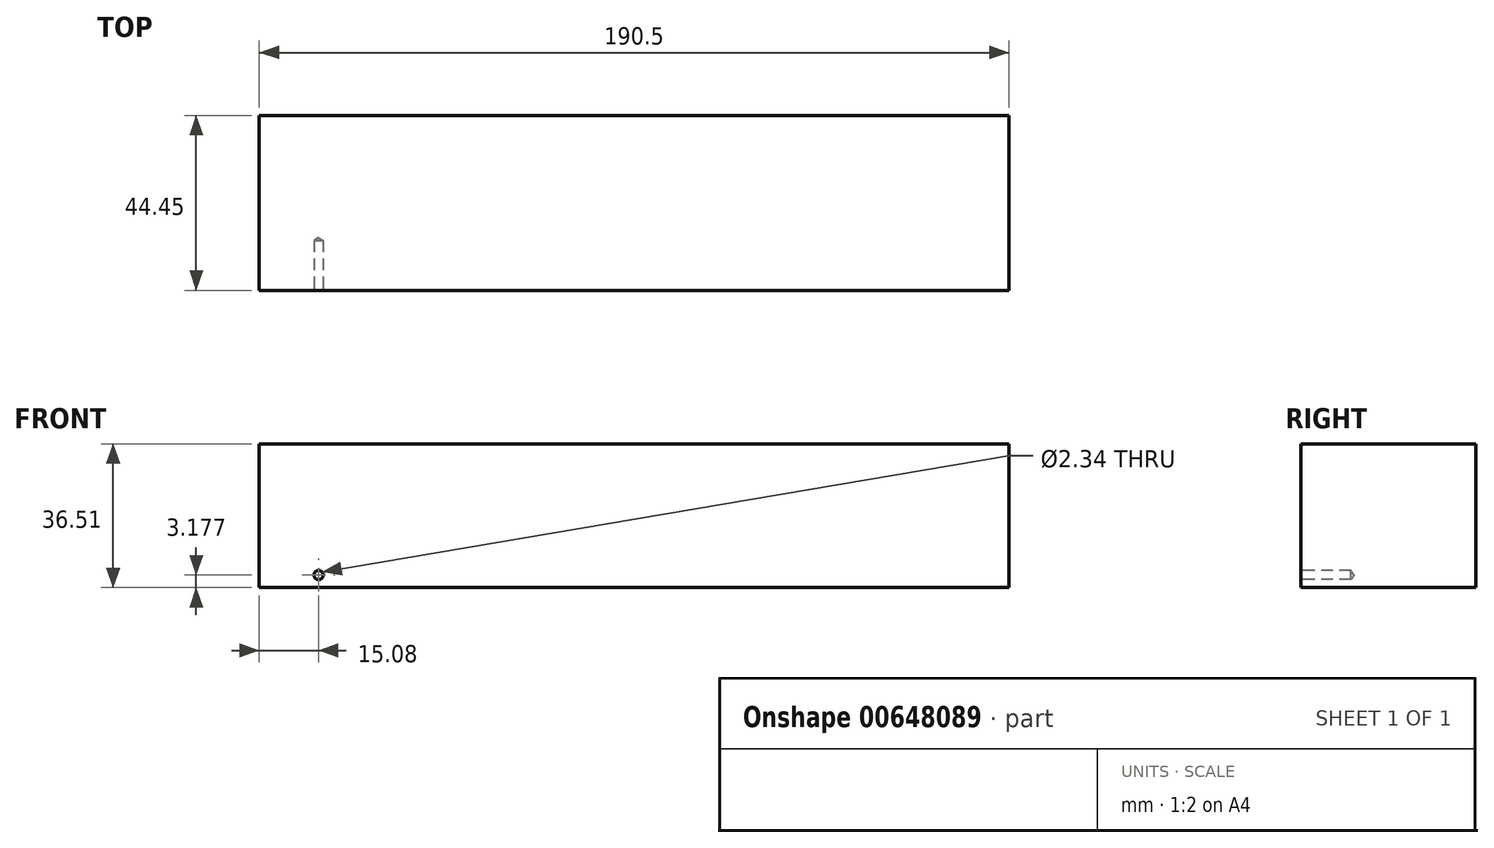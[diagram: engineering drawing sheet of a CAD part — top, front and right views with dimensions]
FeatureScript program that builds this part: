
annotation { "Feature Type Name" : "Feature", "Feature Type Description" : "" }
export const myFeature = defineFeature(function(context is Context, id is Id, definition is map)
    precondition{}
    {
        {
            var Q0;
            Q0=qCreatedBy(makeId("Front.planeOp"),FACE);
            var sketch = newSketch(context, id + "F0", { "sketchPlane" : qUnion([Q0])});
            skLineSegment(sketch, "E0.bottom", {"start": v(-84.15, 8.35) * mm, "end": v(106.35, 8.35) * mm});
            skLineSegment(sketch, "E0.top", {"start": v(-84.15, -28.16) * mm, "end": v(106.35, -28.16) * mm});
            skLineSegment(sketch, "E0.left", {"start": v(-84.15, 8.35) * mm, "end": v(-84.15, -28.16) * mm});
            skLineSegment(sketch, "E0.right", {"start": v(106.35, 8.35) * mm, "end": v(106.35, -28.16) * mm});
            skSolve(sketch);
        }
        {
            var Q0;
            Q0=makeQuery(id+"F0.imprint","IMPRINT",FACE,{"disambiguationData":[TD([[makeQuery(id+"F0.imprint","IMPRINT",EDGE,{"derivedFrom":sQuery(id+"F0.wireOp",EDGE,"E0.bottom")}),-1.0]])]});
            extrude(context, id + "F1", {"entities" : qUnion([Q0]), "depth" : 44.45 * mm, "offsetDistance" : 25.4 * mm});
        }
        {
            var Q0;
            Q0=makeQuery(id+"F1.opExtrude","CAP_FACE",FACE,{"disambiguationData":[OSD([sQuery(id+"F0.wireOp",EDGE,"E0.bottom"),sQuery(id+"F0.wireOp",EDGE,"E0.top"),sQuery(id+"F0.wireOp",EDGE,"E0.left"),sQuery(id+"F0.wireOp",EDGE,"E0.right")])],"isStart":false});
            var sketch = newSketch(context, id + "F2", { "sketchPlane" : qUnion([Q0])});
            skLineSegment(sketch, "E1", {"start": v(-84.15, -28.16) * mm, "end": v(-69.07, -28.16) * mm});
            skLineSegment(sketch, "E2", {"start": v(-69.07, -28.16) * mm, "end": v(-69.07, -38.16) * mm});
            skLineSegment(sketch, "E3", {"start": v(-69.07, -38.16) * mm, "end": v(-69.07, -24.98) * mm});
            skCircle(sketch, "E4", {"center": v(-69.07, -24.98) * mm, "radius": 1.17 * mm});
            skSolve(sketch);
        }
        {
            var Q0;
            Q0=sQuery(id+"F2.wireOp",VERTEX,"E4.center");
            var Q1;
            Q1=makeQuery(id+"F1.opExtrude","SWEPT_BODY",BODY,{"disambiguationData":[OSD([sQuery(id+"F0.wireOp",EDGE,"E0.bottom"),sQuery(id+"F0.wireOp",EDGE,"E0.top"),sQuery(id+"F0.wireOp",EDGE,"E0.left"),sQuery(id+"F0.wireOp",EDGE,"E0.right")])]});
            hole(context, id + "F3", {"style" : HoleStyle.SIMPLE, "endStyle" : HoleEndStyle.BLIND, "holeDiameter" : 2.34 * mm, "majorDiameter" : 6.35 * mm, "holeDepth" : 12.7 * mm, "isTappedThrough" : true, "tappedDepth" : 12.7 * mm, "tapClearance" : 3, "startFromSketch" : true, "locations" : qUnion([Q0]), "scope" : qUnion([Q1])});
        }
    });
